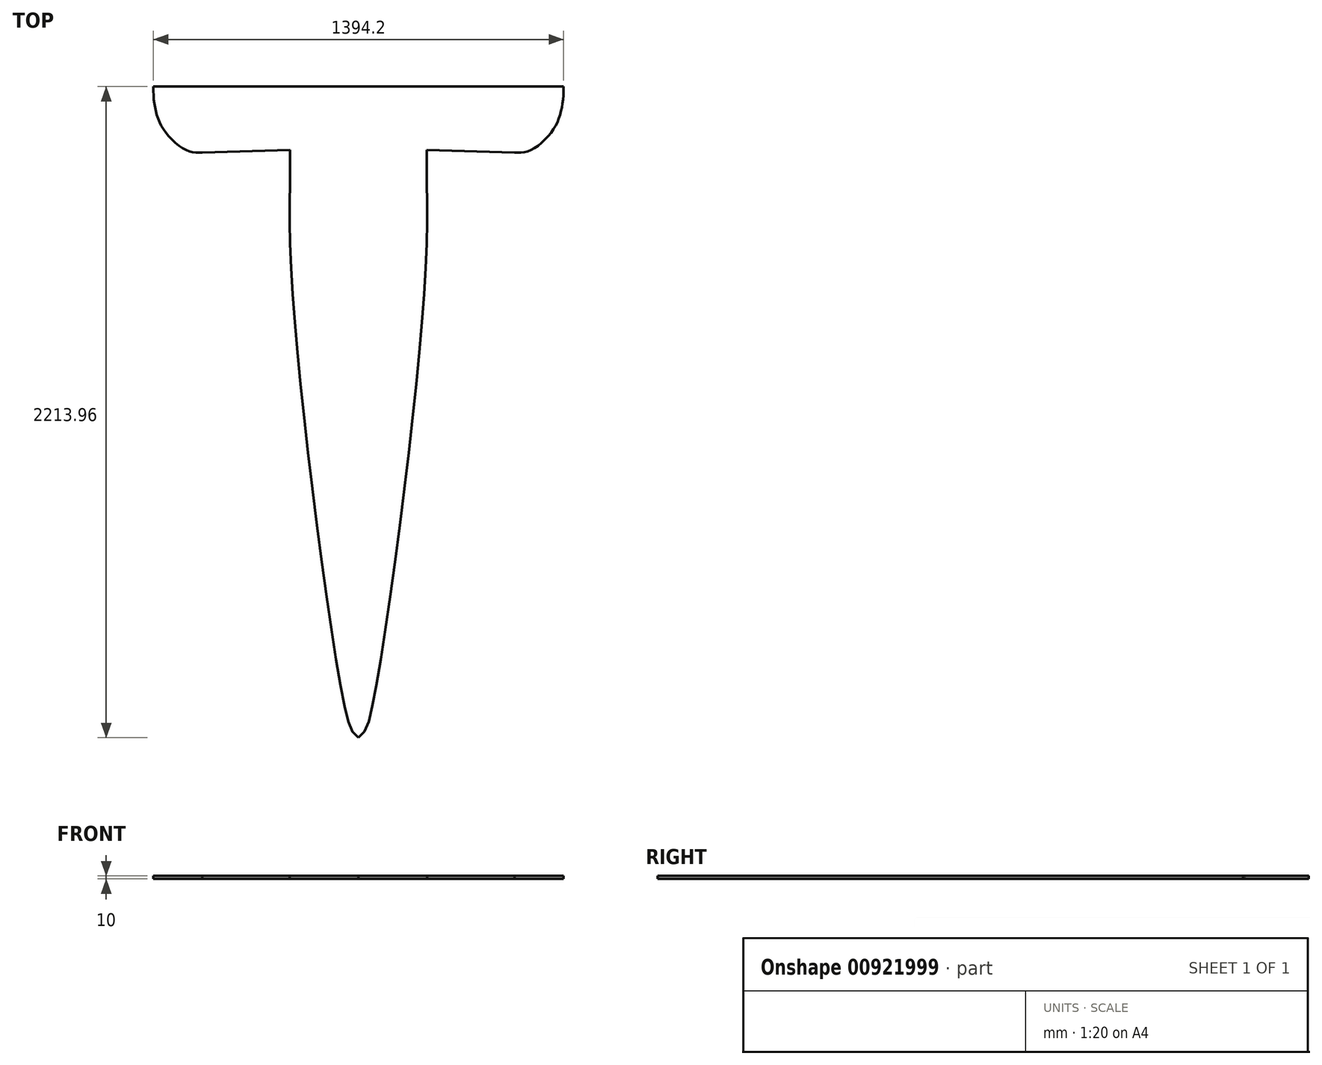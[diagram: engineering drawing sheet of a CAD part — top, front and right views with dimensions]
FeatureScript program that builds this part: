
annotation { "Feature Type Name" : "Feature", "Feature Type Description" : "" }
export const myFeature = defineFeature(function(context is Context, id is Id, definition is map)
    precondition{}
    {
        {
            var Q0;
            Q0=qCreatedBy(makeId("Top.planeOp"),FACE);
            var sketch = newSketch(context, id + "F0", { "sketchPlane" : qUnion([Q0])});
            skLineSegment(sketch, "E0", {"start": v(0, -2128.75) * mm, "end": v(0, 85.2) * mm});
            skLineSegment(sketch, "E1", {"start": v(0, 85.2) * mm, "end": v(697.03, 85.2) * mm});
            skFitSpline(sketch, "E2", {"points": [v(0, -2128.75) * mm, v(44.46, -2035.44) * mm, v(167.74, -1188.8) * mm, v(233, -425.14) * mm, v(232.5, -130.98) * mm], "startDerivative": vector(583.24, 340.8) * mm, "endDerivative": vector(26.16, 1303.17) * mm});
            skLineSegment(sketch, "E3", {"start": v(232.5, -130.98) * mm, "end": v(531.42, -139.24) * mm});
            skFitSpline(sketch, "E4", {"points": [v(697.03, 85.2) * mm, v(688.5, 0) * mm, v(656.18, -69.78) * mm, v(582.87, -132.45) * mm, v(531.42, -139.24) * mm], "startDerivative": vector(6.3, -352.7) * mm, "endDerivative": vector(-249.98, -3.91) * mm});
            skSolve(sketch);
        }
        {
            var Q0;
            Q0=makeQuery(id+"F0.imprint","IMPRINT",FACE,{"disambiguationData":[TD([[makeQuery(id+"F0.imprint","IMPRINT",EDGE,{"derivedFrom":sQuery(id+"F0.wireOp",EDGE,"E0")}),-1.0]])]});
            extrude(context, id + "F1", {"entities" : qUnion([Q0]), "oppositeDirection" : true, "depth" : 10 * mm, "offsetDistance" : 25 * mm});
        }
        {
            var Q0;
            Q0=makeQuery(id+"F1.opExtrude","SWEPT_BODY",BODY,{"disambiguationData":[OSD([sQuery(id+"F0.wireOp",EDGE,"E0"),sQuery(id+"F0.wireOp",EDGE,"E1"),sQuery(id+"F0.wireOp",EDGE,"E2"),sQuery(id+"F0.wireOp",EDGE,"E3"),sQuery(id+"F0.wireOp",EDGE,"E4")])]});
            var Q1;
            Q1=qCreatedBy(makeId("Right.planeOp"),FACE);
            mirror(context, id + "F2", {"operationType" : NewBodyOperationType.ADD, "entities" : qUnion([Q0]), "mirrorPlane" : qUnion([Q1])});
        }
    });
